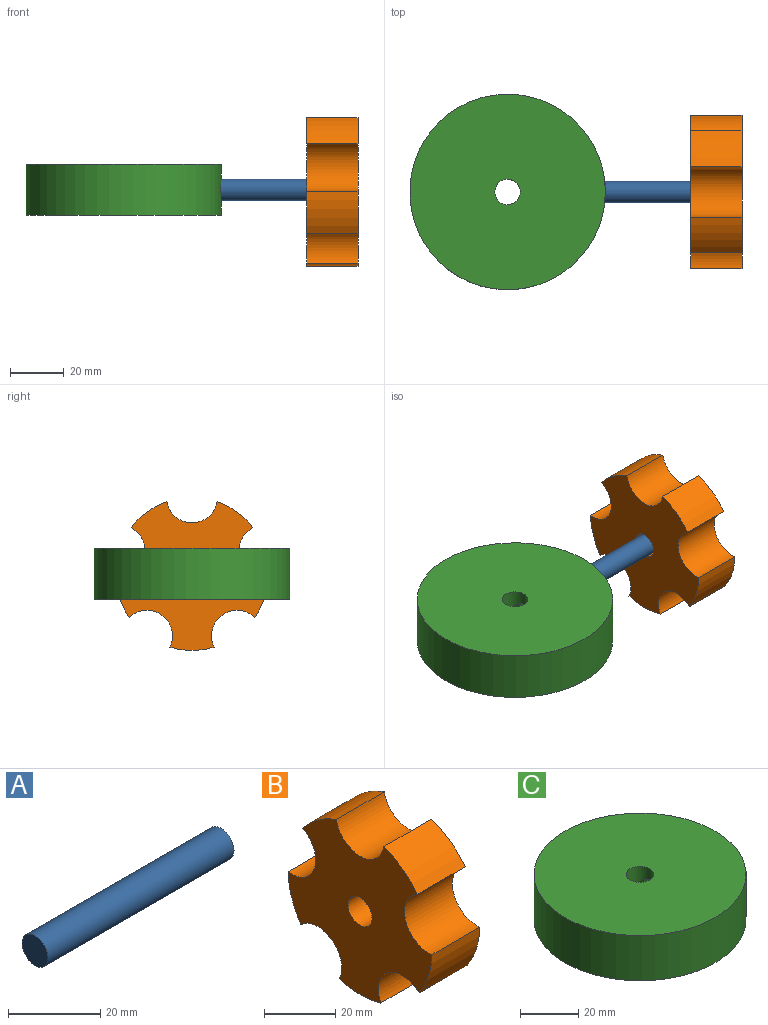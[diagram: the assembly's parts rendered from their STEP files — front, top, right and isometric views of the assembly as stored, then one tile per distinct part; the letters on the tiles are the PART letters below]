
ASSEMBLY  parts=3 mates=2
PART A: 3 faces, bbox 57.2x7.9x7.9 mm
  f0: cylinder r=3.97mm len=57.15mm, axis (-1,0,0), area 1425.1mm2, adj f1,f2
  f1: plane 7.94x7.94mm, normal (1,0,0), area 49.5mm2, adj f0
  f2: plane 7.94x7.94mm, normal (-1,0,0), area 49.5mm2, adj f0
PART B: 14 faces, bbox 19.1x57.1x55.6 mm
  f0: cylinder r=28.57mm len=19.05mm, axis (-1,0,0), area 319.5mm2, adj f5,f6,f7,f11
  f1: cylinder r=28.57mm len=19.05mm, axis (-1,0,0), area 319.5mm2, adj f5,f6,f10,f11
  f2: cylinder r=28.57mm len=19.05mm, axis (-1,0,0), area 319.5mm2, adj f5,f6,f9,f10
  f3: cylinder r=28.57mm len=19.05mm, axis (-1,0,0), area 319.5mm2, adj f5,f6,f8,f9
  f4: cylinder r=28.57mm len=19.05mm, axis (-1,0,0), area 319.5mm2, adj f5,f6,f7,f8
  f5: plane 57.14x55.56mm, normal (1,0,0), area 1903.2mm2, adj f0,f1,f2,f3,f4,f7,f8,f9
  f6: plane 57.14x55.56mm, normal (-1,0,0), area 1831.9mm2, adj f0,f1,f2,f3,f4,f7,f8,f9
  f7: cylinder r=9.53mm len=19.05mm, axis (1,0,0), area 509.3mm2, adj f0,f4,f5,f6
  f8: cylinder r=9.53mm len=19.05mm, axis (1,0,0), area 509.3mm2, adj f3,f4,f5,f6
  f9: cylinder r=9.53mm len=19.05mm, axis (1,0,0), area 509.3mm2, adj f2,f3,f5,f6
  f10: cylinder r=9.53mm len=19.05mm, axis (1,0,0), area 509.3mm2, adj f1,f2,f5,f6
  f11: cylinder r=9.53mm len=19.05mm, axis (1,0,0), area 509.3mm2, adj f0,f1,f5,f6
  f12: cylinder r=4.76mm len=12.7mm, axis (-1,0,0), area 380mm2, adj f6,f13
  f13: plane 9.53x9.53mm, normal (-1,0,0), area 71.3mm2, adj f12
PART C: 5 faces, bbox 73x73x19.1 mm
  f0: cylinder r=36.51mm len=73.03mm, axis (0,0,-1), area 4298.9mm2, adj f1,f2,f4
  f1: plane 73.03x73.03mm, normal (0,0,1), area 4117mm2, adj f0,f3
  f2: plane 73.03x73.03mm, normal (0,0,-1), area 4117mm2, adj f0,f3
  f3: cylinder r=4.76mm len=19.05mm, axis (0,0,1), area 479.3mm2, adj f1,f2,f4
  f4: cylinder r=4.76mm len=36.51mm, axis (1,0,0), area 997.2mm2, adj f0,f3
PLACE A t=(157.37,123.01,-47.21)mm
PLACE B t=(182.77,123.01,-47.21)mm
PLACE C t=(104.76,123.01,-47.21)mm
MATE cylindrical A.f0 <-> C.f4  axis (-1,0,0) through (128.79,123.01,-47.21)mm
MATE cylindrical B.f12 <-> A.f0  axis (-1,0,0) through (185.94,123.01,-47.21)mm
